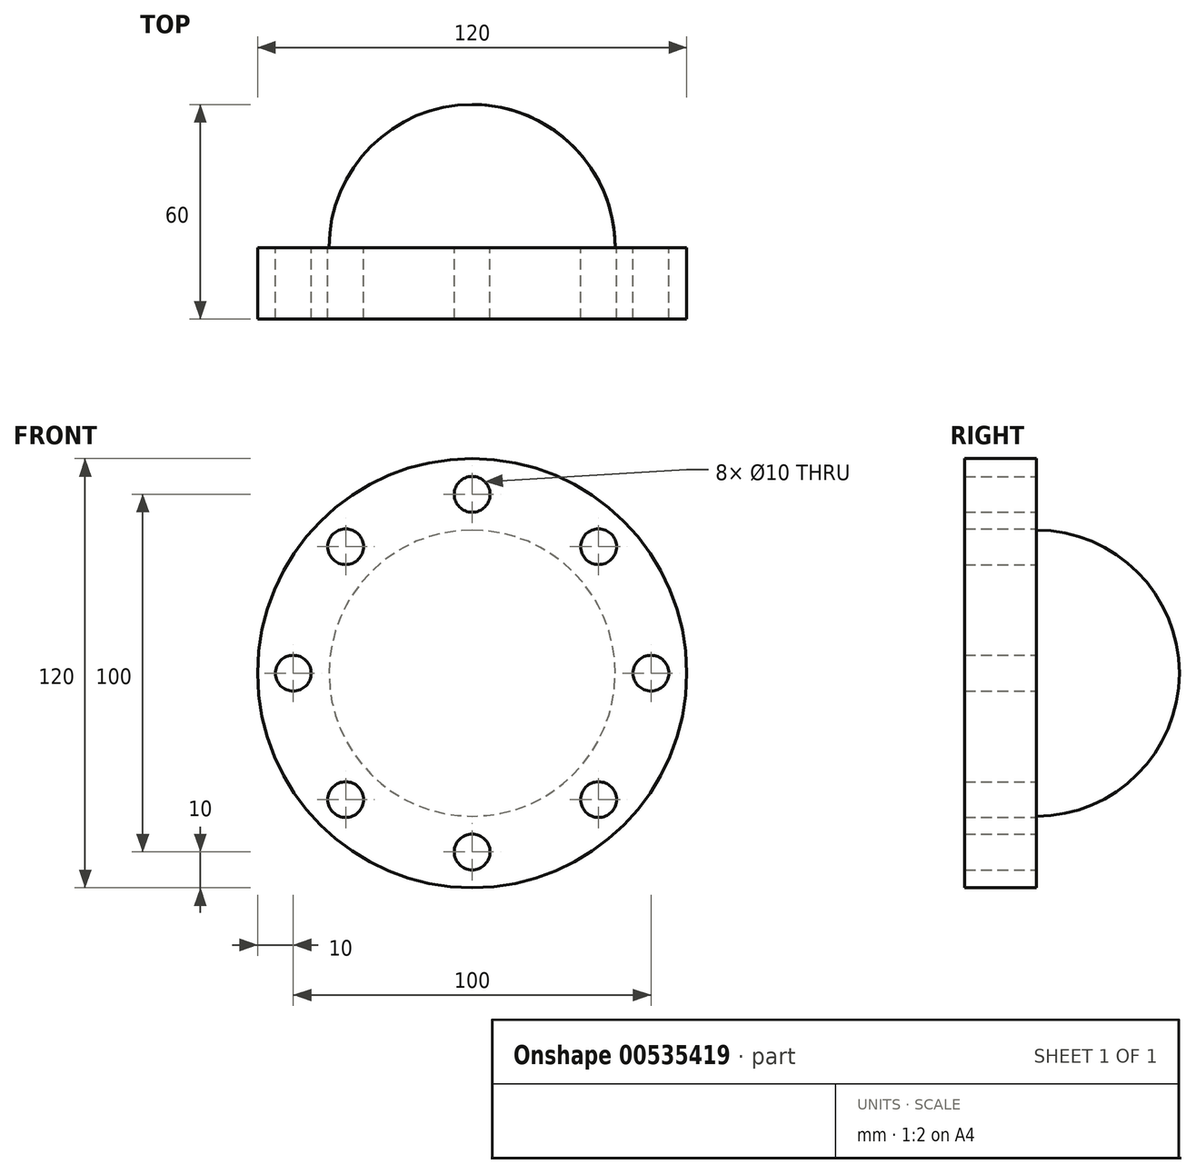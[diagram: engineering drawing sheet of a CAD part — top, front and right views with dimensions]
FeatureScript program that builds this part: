
annotation { "Feature Type Name" : "Feature", "Feature Type Description" : "" }
export const myFeature = defineFeature(function(context is Context, id is Id, definition is map)
    precondition{}
    {
        {
            var Q0;
            Q0=qCreatedBy(makeId("Front.planeOp"),FACE);
            var sketch = newSketch(context, id + "F0", { "sketchPlane" : qUnion([Q0])});
            skCircle(sketch, "E0", {"center": v(0, 0) * mm, "radius": 60 * mm});
            skCircle(sketch, "E1", {"center": v(0, 50) * mm, "radius": 5 * mm});
            skCircle(sketch, "E2.1.0", {"center": v(-35.36, 35.36) * mm, "radius": 5 * mm});
            skCircle(sketch, "E2.2.0", {"center": v(-50, 0) * mm, "radius": 5 * mm});
            skCircle(sketch, "E2.3.0", {"center": v(-35.36, -35.36) * mm, "radius": 5 * mm});
            skCircle(sketch, "E2.4.0", {"center": v(0, -50) * mm, "radius": 5 * mm});
            skCircle(sketch, "E2.5.0", {"center": v(35.36, -35.36) * mm, "radius": 5 * mm});
            skCircle(sketch, "E2.6.0", {"center": v(50, 0) * mm, "radius": 5 * mm});
            skCircle(sketch, "E2.7.0", {"center": v(35.36, 35.36) * mm, "radius": 5 * mm});
            skSolve(sketch);
        }
        {
            var Q0;
            Q0 = qSketchRegion(id + "F0", true);
            extrude(context, id + "F1", {"entities" : qUnion([Q0]), "depth" : 20 * mm, "offsetDistance" : 25 * mm});
        }
        {
            var Q0;
            Q0=qCreatedBy(makeId("Top.planeOp"),FACE);
            var sketch = newSketch(context, id + "F2", { "sketchPlane" : qUnion([Q0])});
            skArc(sketch, "E3", {"start": v(0, 40) * mm, "mid": v(-28.28, 28.28) * mm, "end": v(-40, 0) * mm});
            skLineSegment(sketch, "E4", {"start": v(0, 40) * mm, "end": v(0, 0) * mm});
            skLineSegment(sketch, "E5", {"start": v(0, 0) * mm, "end": v(-40, 0) * mm});
            skSolve(sketch);
        }
        {
            var Q0;
            Q0=makeQuery(id+"F2.imprint","IMPRINT",FACE,{"disambiguationData":[TD([[makeQuery(id+"F2.imprint","IMPRINT",EDGE,{"derivedFrom":sQuery(id+"F2.wireOp",EDGE,"E3")}),1.0]])]});
            var Q1;
            Q1=sQuery(id+"F2.wireOp",EDGE,"E4");
            revolve(context, id + "F3", {"operationType" : NewBodyOperationType.ADD, "entities" : qUnion([Q0]), "axis" : qUnion([Q1]), "revolveType" : RevolveType.FULL});
        }
    });
